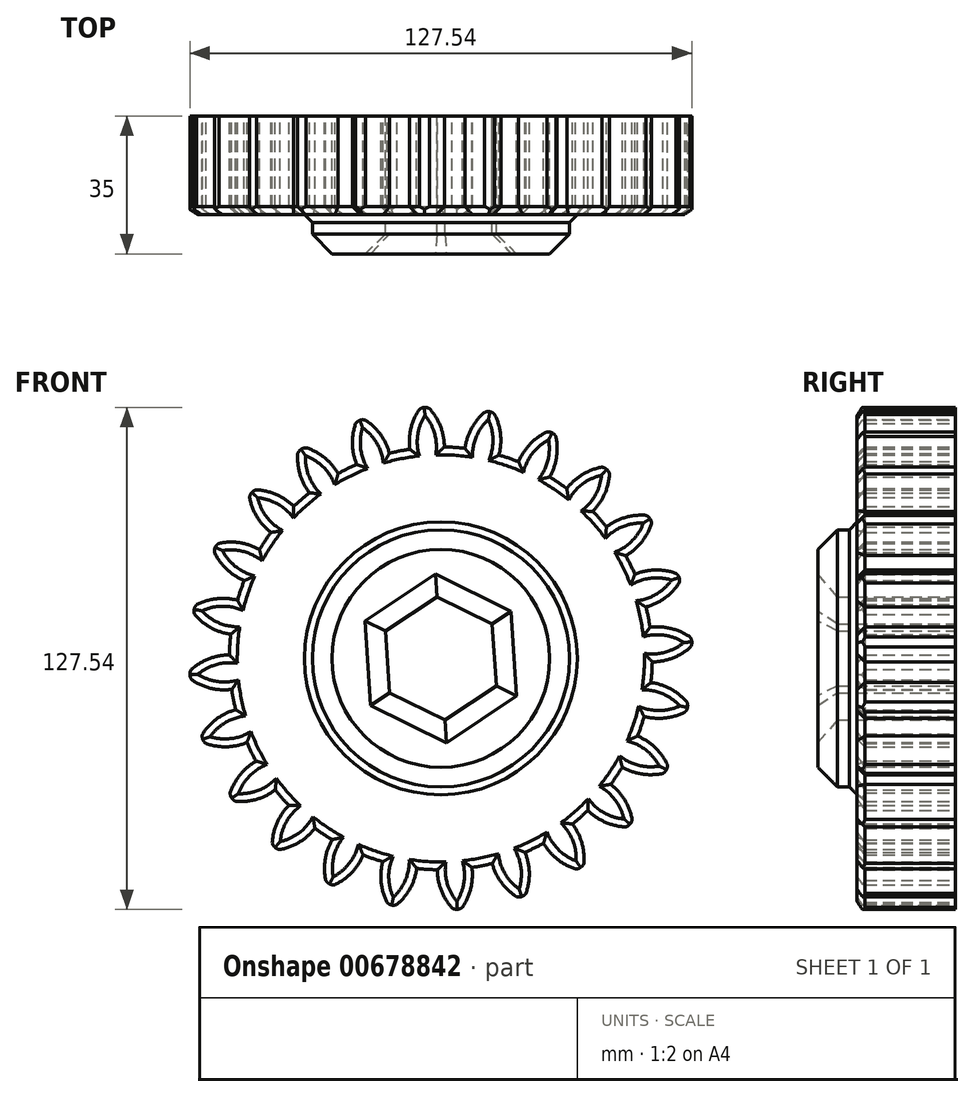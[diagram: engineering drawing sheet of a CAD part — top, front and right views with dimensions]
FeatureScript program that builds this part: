
annotation { "Feature Type Name" : "Feature", "Feature Type Description" : "" }
export const myFeature = defineFeature(function(context is Context, id is Id, definition is map)
    precondition{}
    {
        {
            var Q0;
            Q0=qCreatedBy(makeId("Front.planeOp"),FACE);
            var sketch = newSketch(context, id + "F0", { "sketchPlane" : qUnion([Q0])});
            skCircle(sketch, "E0", {"center": v(0, 0) * mm, "radius": 53.72 * mm});
            skCircle(sketch, "E1", {"center": v(0, 0) * mm, "radius": 58.67 * mm, "construction": true});
            skCircle(sketch, "E2", {"center": v(0, 0) * mm, "radius": 63.5 * mm, "construction": true});
            skLineSegment(sketch, "E3", {"start": v(0, 0) * mm, "end": v(0, 75.2) * mm, "construction": true});
            skLineSegment(sketch, "E4", {"start": v(0, 0) * mm, "end": v(-5.34, 81.5) * mm, "construction": true});
            skLineSegment(sketch, "E5", {"start": v(0, 58.67) * mm, "end": v(-72.87, 58.67) * mm, "construction": true});
            skLineSegment(sketch, "E6", {"start": v(0, 58.67) * mm, "end": v(-71.24, 32.75) * mm, "construction": true});
            skCircle(sketch, "E7", {"center": v(0, 0) * mm, "radius": 55.14 * mm, "construction": true});
            skCircle(sketch, "E8", {"center": v(0, 58.67) * mm, "radius": 14.6 * mm, "construction": true});
            skCircle(sketch, "E9", {"center": v(-13.72, 53.68) * mm, "radius": 14.6 * mm, "construction": true});
            skArc(sketch, "E10", {"start": v(0, 58.67) * mm, "mid": v(-1.2, 61.2) * mm, "end": v(-2.86, 63.44) * mm});
            skArc(sketch, "E11", {"start": v(0.88, 53.71) * mm, "mid": v(0.66, 56.23) * mm, "end": v(0, 58.67) * mm});
            skArc(sketch, "E12.MirrorCS", {"start": v(-7.88, 53.14) * mm, "mid": v(-8, 55.67) * mm, "end": v(-7.66, 58.17) * mm});
            skArc(sketch, "E13.MirrorCS", {"start": v(-7.66, 58.17) * mm, "mid": v(-6.8, 60.82) * mm, "end": v(-5.45, 63.27) * mm});
            skArc(sketch, "E14", {"start": v(-2.86, 63.44) * mm, "mid": v(-4.18, 63.76) * mm, "end": v(-5.45, 63.27) * mm});
            skCircle(sketch, "E15", {"center": v(0, 0) * mm, "radius": 32.66 * mm});
            skCircle(sketch, "E16.cCircle", {"center": v(0, 0) * mm, "radius": 15.7 * mm, "construction": true});
            skLineSegment(sketch, "E16.0", {"start": v(-1.03, 15.66) * mm, "end": v(13.05, 8.72) * mm});
            skLineSegment(sketch, "E16.1", {"start": v(13.05, 8.72) * mm, "end": v(14.08, -6.94) * mm});
            skLineSegment(sketch, "E16.2", {"start": v(14.08, -6.94) * mm, "end": v(1.03, -15.66) * mm});
            skLineSegment(sketch, "E16.3", {"start": v(1.03, -15.66) * mm, "end": v(-13.05, -8.72) * mm});
            skLineSegment(sketch, "E16.4", {"start": v(-13.05, -8.72) * mm, "end": v(-14.08, 6.94) * mm});
            skLineSegment(sketch, "E16.5", {"start": v(-14.08, 6.94) * mm, "end": v(-1.03, 15.66) * mm});
            skSolve(sketch);
        }
        {
            var Q0;
            {var subQ0=sQuery(id+"F0.wireOp",EDGE,"E0");var subQ1=makeQuery(id+"F0.imprint","INTERSECT",VERTEX,{"derivedFrom":[subQ0,sQuery(id+"F0.wireOp",EDGE,"E11")]});Q0=makeQuery(id+"F0.imprint","IMPRINT",FACE,{"disambiguationData":[TD([[makeQuery(id+"F0.imprint","IMPRINT",EDGE,{"disambiguationData":[TD([[subQ1,-1.0]])],"derivedFrom":subQ0}),1.0]])]});}
            var Q1;
            Q1=makeQuery(id+"F0.imprint","IMPRINT",FACE,{"disambiguationData":[TD([[makeQuery(id+"F0.imprint","IMPRINT",EDGE,{"derivedFrom":sQuery(id+"F0.wireOp",EDGE,"E10")}),1.0]])]});
            extrude(context, id + "F1", {"entities" : qUnion([Q0, Q1]), "depth" : 25 * mm, "offsetDistance" : 25 * mm});
        }
        {
            var Q0;
            Q0=makeQuery(id+"F1.opExtrude","SWEPT_BODY",BODY,{"disambiguationData":[OSD([sQuery(id+"F0.wireOp",EDGE,"E0"),sQuery(id+"F0.wireOp",EDGE,"E10"),sQuery(id+"F0.wireOp",EDGE,"E11"),sQuery(id+"F0.wireOp",EDGE,"E12.MirrorCS"),sQuery(id+"F0.wireOp",EDGE,"E13.MirrorCS"),sQuery(id+"F0.wireOp",EDGE,"E14")])]});
            var Q1;
            Q1=makeQuery(id+"F1.opExtrude","SWEPT_FACE",FACE,{"disambiguationData":[OSD([sQuery(id+"F0.wireOp",EDGE,"E0")])]});
            circularPattern(context, id + "F2", {"entities" : qUnion([Q0]), "axis" : qUnion([Q1]), "angle" : 360 * degree, "instanceCount" : 24, "equalSpace" : true});
        }
        {
            var Q0;
            Q0=makeQuery(id+"F0.imprint","IMPRINT",FACE,{"disambiguationData":[TD([[makeQuery(id+"F0.imprint","IMPRINT",EDGE,{"derivedFrom":sQuery(id+"F0.wireOp",EDGE,"E15")}),1.0]])]});
            extrude(context, id + "F3", {"entities" : qUnion([Q0]), "operationType" : NewBodyOperationType.ADD, "depth" : 35 * mm, "offsetDistance" : 25 * mm});
        }
        {
            var Q0;
            Q0=makeQuery(id+"F3.opExtrude","CAP_FACE",FACE,{"disambiguationData":[OSD([sQuery(id+"F0.wireOp",EDGE,"E15"),sQuery(id+"F0.wireOp",EDGE,"E16.0"),sQuery(id+"F0.wireOp",EDGE,"E16.1"),sQuery(id+"F0.wireOp",EDGE,"E16.2"),sQuery(id+"F0.wireOp",EDGE,"E16.3"),sQuery(id+"F0.wireOp",EDGE,"E16.4"),sQuery(id+"F0.wireOp",EDGE,"E16.5")])],"isStart":false});
            chamfer(context, id + "F4", {"entities" : qUnion([Q0]), "width" : 5 * mm, "tangentPropagation" : true});
        }
        {
            var Q0;
            Q0=makeQuery(id+"F2.opPattern","COPY",EDGE,{"derivedFrom":makeQuery(id+"F1.opExtrude","CAP_EDGE",EDGE,{"disambiguationData":[OSD([sQuery(id+"F0.wireOp",EDGE,"E14")])],"isStart":false}),"instanceName":"21"});
            var Q1;
            Q1=makeQuery(id+"F2.opPattern","COPY",EDGE,{"derivedFrom":makeQuery(id+"F1.opExtrude","CAP_EDGE",EDGE,{"disambiguationData":[OSD([sQuery(id+"F0.wireOp",EDGE,"E10")])],"isStart":false}),"instanceName":"21"});
            var Q2;
            Q2=makeQuery(id+"F2.opPattern","COPY",EDGE,{"derivedFrom":makeQuery(id+"F1.opExtrude","CAP_EDGE",EDGE,{"disambiguationData":[OSD([sQuery(id+"F0.wireOp",EDGE,"E11")])],"isStart":false}),"instanceName":"21"});
            var Q3;
            Q3=makeQuery(id+"F2.opPattern","COPY",EDGE,{"derivedFrom":makeQuery(id+"F1.opExtrude","CAP_EDGE",EDGE,{"disambiguationData":[OSD([sQuery(id+"F0.wireOp",EDGE,"E13.MirrorCS")])],"isStart":false}),"instanceName":"21"});
            var Q4;
            Q4=makeQuery(id+"F2.opPattern","COPY",EDGE,{"derivedFrom":makeQuery(id+"F1.opExtrude","CAP_EDGE",EDGE,{"disambiguationData":[OSD([sQuery(id+"F0.wireOp",EDGE,"E12.MirrorCS")])],"isStart":false}),"instanceName":"21"});
            var Q5;
            Q5=makeQuery(id+"F1.opExtrude","CAP_EDGE",EDGE,{"disambiguationData":[OSD([sQuery(id+"F0.wireOp",EDGE,"E14")])],"isStart":false});
            var Q6;
            Q6=makeQuery(id+"F1.opExtrude","CAP_EDGE",EDGE,{"disambiguationData":[OSD([sQuery(id+"F0.wireOp",EDGE,"E13.MirrorCS")])],"isStart":false});
            var Q7;
            Q7=makeQuery(id+"F1.opExtrude","CAP_EDGE",EDGE,{"disambiguationData":[OSD([sQuery(id+"F0.wireOp",EDGE,"E10")])],"isStart":false});
            var Q8;
            Q8=makeQuery(id+"F1.opExtrude","CAP_EDGE",EDGE,{"disambiguationData":[OSD([sQuery(id+"F0.wireOp",EDGE,"E12.MirrorCS")])],"isStart":false});
            var Q9;
            Q9=makeQuery(id+"F1.opExtrude","CAP_EDGE",EDGE,{"disambiguationData":[OSD([sQuery(id+"F0.wireOp",EDGE,"E11")])],"isStart":false});
            var Q10;
            Q10=makeQuery(id+"F2.opPattern","COPY",EDGE,{"derivedFrom":makeQuery(id+"F1.opExtrude","CAP_EDGE",EDGE,{"disambiguationData":[OSD([sQuery(id+"F0.wireOp",EDGE,"E13.MirrorCS")])],"isStart":false}),"instanceName":"22"});
            var Q11;
            Q11=makeQuery(id+"F2.opPattern","COPY",EDGE,{"derivedFrom":makeQuery(id+"F1.opExtrude","CAP_EDGE",EDGE,{"disambiguationData":[OSD([sQuery(id+"F0.wireOp",EDGE,"E14")])],"isStart":false}),"instanceName":"22"});
            var Q12;
            Q12=makeQuery(id+"F2.opPattern","COPY",EDGE,{"derivedFrom":makeQuery(id+"F1.opExtrude","CAP_EDGE",EDGE,{"disambiguationData":[OSD([sQuery(id+"F0.wireOp",EDGE,"E12.MirrorCS")])],"isStart":false}),"instanceName":"22"});
            var Q13;
            Q13=makeQuery(id+"F2.opPattern","COPY",EDGE,{"derivedFrom":makeQuery(id+"F1.opExtrude","CAP_EDGE",EDGE,{"disambiguationData":[OSD([sQuery(id+"F0.wireOp",EDGE,"E10")])],"isStart":false}),"instanceName":"22"});
            var Q14;
            Q14=makeQuery(id+"F2.opPattern","COPY",EDGE,{"derivedFrom":makeQuery(id+"F1.opExtrude","CAP_EDGE",EDGE,{"disambiguationData":[OSD([sQuery(id+"F0.wireOp",EDGE,"E11")])],"isStart":false}),"instanceName":"22"});
            var Q15;
            Q15=makeQuery(id+"F2.opPattern","COPY",EDGE,{"derivedFrom":makeQuery(id+"F1.opExtrude","CAP_EDGE",EDGE,{"disambiguationData":[OSD([sQuery(id+"F0.wireOp",EDGE,"E13.MirrorCS")])],"isStart":false}),"instanceName":"23"});
            var Q16;
            Q16=makeQuery(id+"F2.opPattern","COPY",EDGE,{"derivedFrom":makeQuery(id+"F1.opExtrude","CAP_EDGE",EDGE,{"disambiguationData":[OSD([sQuery(id+"F0.wireOp",EDGE,"E14")])],"isStart":false}),"instanceName":"23"});
            var Q17;
            Q17=makeQuery(id+"F2.opPattern","COPY",EDGE,{"derivedFrom":makeQuery(id+"F1.opExtrude","CAP_EDGE",EDGE,{"disambiguationData":[OSD([sQuery(id+"F0.wireOp",EDGE,"E10")])],"isStart":false}),"instanceName":"23"});
            var Q18;
            Q18=makeQuery(id+"F2.opPattern","COPY",EDGE,{"derivedFrom":makeQuery(id+"F1.opExtrude","CAP_EDGE",EDGE,{"disambiguationData":[OSD([sQuery(id+"F0.wireOp",EDGE,"E11")])],"isStart":false}),"instanceName":"23"});
            var Q19;
            Q19=makeQuery(id+"F2.opPattern","COPY",EDGE,{"derivedFrom":makeQuery(id+"F1.opExtrude","CAP_EDGE",EDGE,{"disambiguationData":[OSD([sQuery(id+"F0.wireOp",EDGE,"E12.MirrorCS")])],"isStart":false}),"instanceName":"23"});
            var Q20;
            Q20=makeQuery(id+"F2.opPattern","COPY",EDGE,{"derivedFrom":makeQuery(id+"F1.opExtrude","CAP_EDGE",EDGE,{"disambiguationData":[OSD([sQuery(id+"F0.wireOp",EDGE,"E14")])],"isStart":false}),"instanceName":"20"});
            var Q21;
            Q21=makeQuery(id+"F2.opPattern","COPY",EDGE,{"derivedFrom":makeQuery(id+"F1.opExtrude","CAP_EDGE",EDGE,{"disambiguationData":[OSD([sQuery(id+"F0.wireOp",EDGE,"E10")])],"isStart":false}),"instanceName":"20"});
            var Q22;
            Q22=makeQuery(id+"F2.opPattern","COPY",EDGE,{"derivedFrom":makeQuery(id+"F1.opExtrude","CAP_EDGE",EDGE,{"disambiguationData":[OSD([sQuery(id+"F0.wireOp",EDGE,"E11")])],"isStart":false}),"instanceName":"20"});
            var Q23;
            Q23=makeQuery(id+"F2.opPattern","COPY",EDGE,{"derivedFrom":makeQuery(id+"F1.opExtrude","CAP_EDGE",EDGE,{"disambiguationData":[OSD([sQuery(id+"F0.wireOp",EDGE,"E13.MirrorCS")])],"isStart":false}),"instanceName":"20"});
            var Q24;
            Q24=makeQuery(id+"F2.opPattern","COPY",EDGE,{"derivedFrom":makeQuery(id+"F1.opExtrude","CAP_EDGE",EDGE,{"disambiguationData":[OSD([sQuery(id+"F0.wireOp",EDGE,"E12.MirrorCS")])],"isStart":false}),"instanceName":"20"});
            var Q25;
            Q25=makeQuery(id+"F2.opPattern","COPY",EDGE,{"derivedFrom":makeQuery(id+"F1.opExtrude","CAP_EDGE",EDGE,{"disambiguationData":[OSD([sQuery(id+"F0.wireOp",EDGE,"E10")])],"isStart":false}),"instanceName":"19"});
            var Q26;
            Q26=makeQuery(id+"F2.opPattern","COPY",EDGE,{"derivedFrom":makeQuery(id+"F1.opExtrude","CAP_EDGE",EDGE,{"disambiguationData":[OSD([sQuery(id+"F0.wireOp",EDGE,"E11")])],"isStart":false}),"instanceName":"19"});
            var Q27;
            Q27=makeQuery(id+"F2.opPattern","COPY",EDGE,{"derivedFrom":makeQuery(id+"F1.opExtrude","CAP_EDGE",EDGE,{"disambiguationData":[OSD([sQuery(id+"F0.wireOp",EDGE,"E14")])],"isStart":false}),"instanceName":"19"});
            var Q28;
            Q28=makeQuery(id+"F2.opPattern","COPY",EDGE,{"derivedFrom":makeQuery(id+"F1.opExtrude","CAP_EDGE",EDGE,{"disambiguationData":[OSD([sQuery(id+"F0.wireOp",EDGE,"E13.MirrorCS")])],"isStart":false}),"instanceName":"19"});
            var Q29;
            Q29=makeQuery(id+"F2.opPattern","COPY",EDGE,{"derivedFrom":makeQuery(id+"F1.opExtrude","CAP_EDGE",EDGE,{"disambiguationData":[OSD([sQuery(id+"F0.wireOp",EDGE,"E12.MirrorCS")])],"isStart":false}),"instanceName":"19"});
            var Q30;
            Q30=makeQuery(id+"F2.opPattern","COPY",EDGE,{"derivedFrom":makeQuery(id+"F1.opExtrude","CAP_EDGE",EDGE,{"disambiguationData":[OSD([sQuery(id+"F0.wireOp",EDGE,"E14")])],"isStart":false}),"instanceName":"18"});
            var Q31;
            Q31=makeQuery(id+"F2.opPattern","COPY",EDGE,{"derivedFrom":makeQuery(id+"F1.opExtrude","CAP_EDGE",EDGE,{"disambiguationData":[OSD([sQuery(id+"F0.wireOp",EDGE,"E13.MirrorCS")])],"isStart":false}),"instanceName":"18"});
            var Q32;
            Q32=makeQuery(id+"F2.opPattern","COPY",EDGE,{"derivedFrom":makeQuery(id+"F1.opExtrude","CAP_EDGE",EDGE,{"disambiguationData":[OSD([sQuery(id+"F0.wireOp",EDGE,"E12.MirrorCS")])],"isStart":false}),"instanceName":"18"});
            var Q33;
            Q33=makeQuery(id+"F2.opPattern","COPY",EDGE,{"derivedFrom":makeQuery(id+"F1.opExtrude","CAP_EDGE",EDGE,{"disambiguationData":[OSD([sQuery(id+"F0.wireOp",EDGE,"E10")])],"isStart":false}),"instanceName":"18"});
            var Q34;
            {var subQ0=makeQuery(id+"F1.opExtrude","CAP_FACE",FACE,{"disambiguationData":[OSD([sQuery(id+"F0.wireOp",EDGE,"E0"),sQuery(id+"F0.wireOp",EDGE,"E10"),sQuery(id+"F0.wireOp",EDGE,"E11"),sQuery(id+"F0.wireOp",EDGE,"E12.MirrorCS"),sQuery(id+"F0.wireOp",EDGE,"E13.MirrorCS"),sQuery(id+"F0.wireOp",EDGE,"E14"),sQuery(id+"F0.wireOp",EDGE,"E15")])],"isStart":false});Q34=makeQuery(id+"F3.boolean.opBoolean","MERGE",FACE,{"derivedFrom":[subQ0,makeQuery(id+"F2.opPattern","COPY",FACE,{"derivedFrom":subQ0,"instanceName":"1"}),makeQuery(id+"F2.opPattern","COPY",FACE,{"derivedFrom":subQ0,"instanceName":"2"}),makeQuery(id+"F2.opPattern","COPY",FACE,{"derivedFrom":subQ0,"instanceName":"3"}),makeQuery(id+"F2.opPattern","COPY",FACE,{"derivedFrom":subQ0,"instanceName":"4"}),makeQuery(id+"F2.opPattern","COPY",FACE,{"derivedFrom":subQ0,"instanceName":"5"}),makeQuery(id+"F2.opPattern","COPY",FACE,{"derivedFrom":subQ0,"instanceName":"6"}),makeQuery(id+"F2.opPattern","COPY",FACE,{"derivedFrom":subQ0,"instanceName":"7"}),makeQuery(id+"F2.opPattern","COPY",FACE,{"derivedFrom":subQ0,"instanceName":"8"}),makeQuery(id+"F2.opPattern","COPY",FACE,{"derivedFrom":subQ0,"instanceName":"9"}),makeQuery(id+"F2.opPattern","COPY",FACE,{"derivedFrom":subQ0,"instanceName":"10"}),makeQuery(id+"F2.opPattern","COPY",FACE,{"derivedFrom":subQ0,"instanceName":"11"}),makeQuery(id+"F2.opPattern","COPY",FACE,{"derivedFrom":subQ0,"instanceName":"12"}),makeQuery(id+"F2.opPattern","COPY",FACE,{"derivedFrom":subQ0,"instanceName":"13"}),makeQuery(id+"F2.opPattern","COPY",FACE,{"derivedFrom":subQ0,"instanceName":"14"}),makeQuery(id+"F2.opPattern","COPY",FACE,{"derivedFrom":subQ0,"instanceName":"15"}),makeQuery(id+"F2.opPattern","COPY",FACE,{"derivedFrom":subQ0,"instanceName":"16"}),makeQuery(id+"F2.opPattern","COPY",FACE,{"derivedFrom":subQ0,"instanceName":"17"}),makeQuery(id+"F2.opPattern","COPY",FACE,{"derivedFrom":subQ0,"instanceName":"18"}),makeQuery(id+"F2.opPattern","COPY",FACE,{"derivedFrom":subQ0,"instanceName":"19"}),makeQuery(id+"F2.opPattern","COPY",FACE,{"derivedFrom":subQ0,"instanceName":"20"}),makeQuery(id+"F2.opPattern","COPY",FACE,{"derivedFrom":subQ0,"instanceName":"21"}),makeQuery(id+"F2.opPattern","COPY",FACE,{"derivedFrom":subQ0,"instanceName":"22"}),makeQuery(id+"F2.opPattern","COPY",FACE,{"derivedFrom":subQ0,"instanceName":"23"})]});}
            chamfer(context, id + "F5", {"entities" : qUnion([Q0, Q1, Q2, Q3, Q4, Q5, Q6, Q7, Q8, Q9, Q10, Q11, Q12, Q13, Q14, Q15, Q16, Q17, Q18, Q19, Q20, Q21, Q22, Q23, Q24, Q25, Q26, Q27, Q28, Q29, Q30, Q31, Q32, Q33, Q34]), "width" : 2 * mm, "tangentPropagation" : true});
        }
    });
